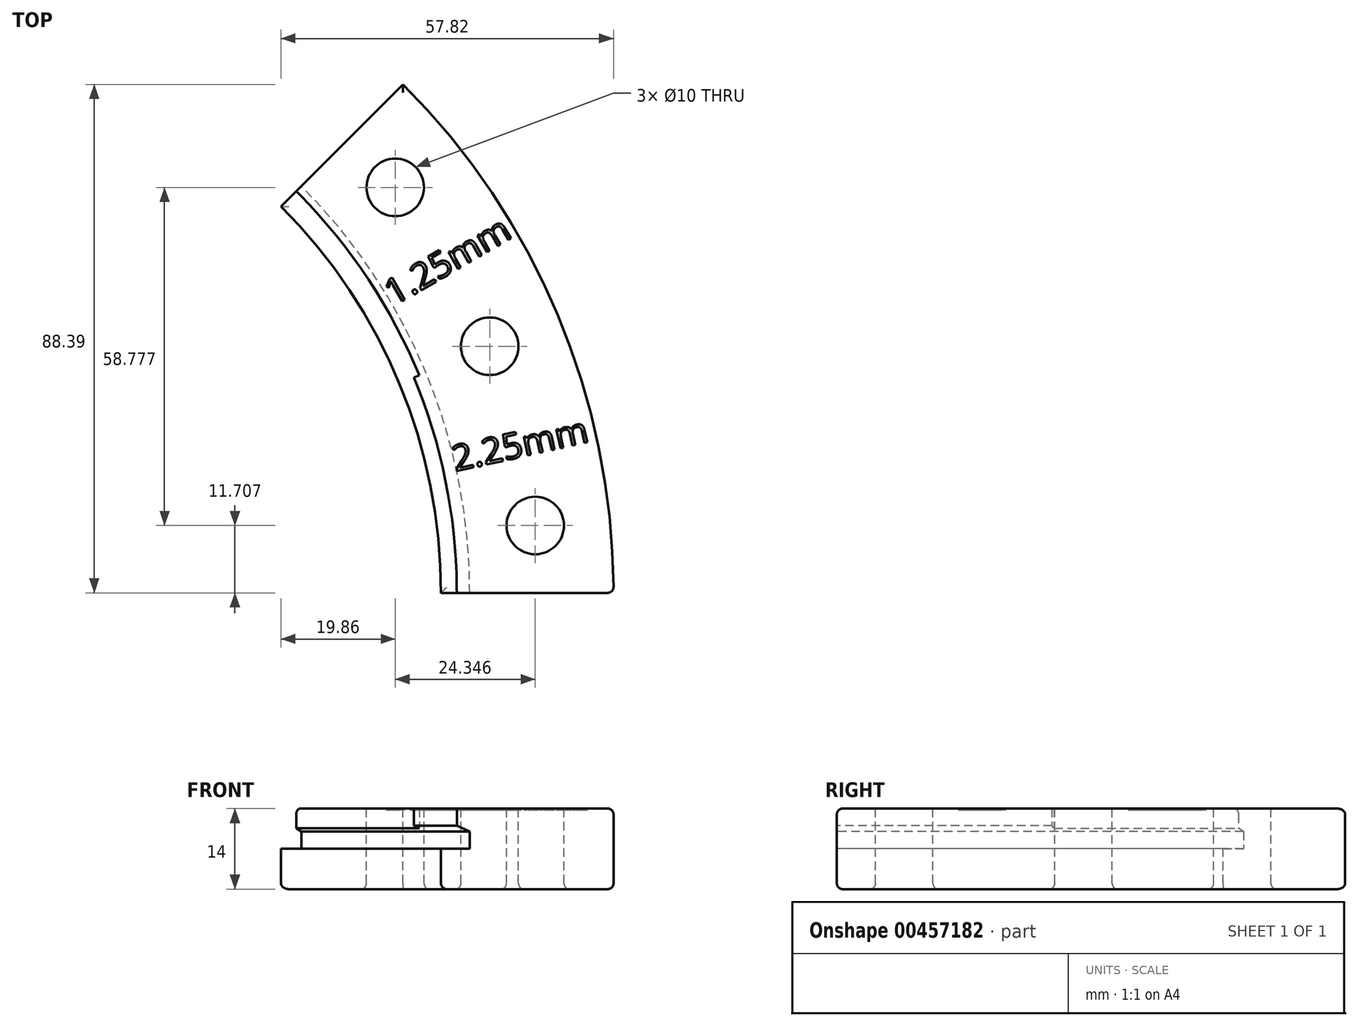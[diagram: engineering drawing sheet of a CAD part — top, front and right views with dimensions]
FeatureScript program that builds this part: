
annotation { "Feature Type Name" : "Feature", "Feature Type Description" : "" }
export const myFeature = defineFeature(function(context is Context, id is Id, definition is map)
    precondition{}
    {
        {
            var Q0;
            Q0=qCreatedBy(makeId("Top.planeOp"),FACE);
            var sketch = newSketch(context, id + "F0", { "sketchPlane" : qUnion([Q0])});
            skCircle(sketch, "E0", {"center": v(0, 0) * mm, "radius": 100 * mm});
            skSolve(sketch);
        }
        {
            var Q0;
            Q0=qCreatedBy(makeId("Front.planeOp"),FACE);
            var sketch = newSketch(context, id + "F1", { "sketchPlane" : qUnion([Q0])});
            skLineSegment(sketch, "E1.0", {"start": v(-100, 0) * mm, "end": v(100, 0) * mm});
            skLineSegment(sketch, "E2", {"start": v(100, 4) * mm, "end": v(97.75, 4) * mm});
            skLineSegment(sketch, "E3", {"start": v(125, 4) * mm, "end": v(100, 4) * mm});
            skLineSegment(sketch, "E4", {"start": v(100, 0) * mm, "end": v(100, -3) * mm});
            skLineSegment(sketch, "E5", {"start": v(100, -10) * mm, "end": v(125, -10) * mm});
            skLineSegment(sketch, "E6", {"start": v(125, -10) * mm, "end": v(125, 4) * mm});
            skLineSegment(sketch, "E7", {"start": v(0, 0) * mm, "end": v(0, 50.74) * mm});
            skLineSegment(sketch, "E8", {"start": v(100, -10) * mm, "end": v(95, -10) * mm});
            skLineSegment(sketch, "E9", {"start": v(95, -10) * mm, "end": v(95, -3) * mm});
            skLineSegment(sketch, "E10", {"start": v(95, -3) * mm, "end": v(100, -3) * mm});
            skLineSegment(sketch, "E11", {"start": v(97.75, 4) * mm, "end": v(97.75, 1) * mm});
            skLineSegment(sketch, "E12", {"start": v(100, 0) * mm, "end": v(97.75, 1) * mm});
            skSolve(sketch);
        }
        {
            var Q0;
            Q0=makeQuery(id+"F1.imprint","IMPRINT",FACE,{"disambiguationData":[TD([[makeQuery(id+"F1.imprint","IMPRINT",EDGE,{"derivedFrom":sQuery(id+"F1.wireOp",EDGE,"E2")}),1.0]])]});
            var Q1;
            Q1=sQuery(id+"F1.wireOp",EDGE,"E7");
            revolve(context, id + "F2", {"entities" : qUnion([Q0]), "axis" : qUnion([Q1]), "revolveType" : RevolveType.ONE_DIRECTION, "angle" : 45 * degree});
        }
        {
            var Q0;
            Q0=makeQuery(id+"F2.opRevolve","CAP_FACE",FACE,{"disambiguationData":[OSD([sQuery(id+"F1.wireOp",EDGE,"E2"),sQuery(id+"F1.wireOp",EDGE,"E3"),sQuery(id+"F1.wireOp",EDGE,"E4"),sQuery(id+"F1.wireOp",EDGE,"E5"),sQuery(id+"F1.wireOp",EDGE,"E6"),sQuery(id+"F1.wireOp",EDGE,"E8"),sQuery(id+"F1.wireOp",EDGE,"E9"),sQuery(id+"F1.wireOp",EDGE,"E10"),sQuery(id+"F1.wireOp",EDGE,"E11"),sQuery(id+"F1.wireOp",EDGE,"E12")])],"isStart":false});
            var sketch = newSketch(context, id + "F3", { "sketchPlane" : qUnion([Q0])});
            skLineSegment(sketch, "E13", {"start": v(0, 0) * mm, "end": v(0, 46.88) * mm});
            skLineSegment(sketch, "E14.0", {"start": v(-98.75, 0.56) * mm, "end": v(-97.75, 1) * mm});
            skLineSegment(sketch, "E15.0", {"start": v(-97.75, 4) * mm, "end": v(-97.75, 1) * mm});
            skLineSegment(sketch, "E16.0", {"start": v(-98.75, 4) * mm, "end": v(-97.75, 4) * mm});
            skLineSegment(sketch, "E17", {"start": v(-98.75, 4) * mm, "end": v(-98.75, 0.56) * mm});
            skLineSegment(sketch, "E18", {"start": v(-97.75, 4) * mm, "end": v(-98.75, 4) * mm});
            skPoint(sketch, "E19.start.orphan", {"position": v(-100, 0) * mm});
            skPoint(sketch, "E20.orphan", {"position": v(-125, 4) * mm});
            skSolve(sketch);
        }
        {
            var Q0;
            Q0=makeQuery(id+"F3.imprint","IMPRINT",FACE,{"disambiguationData":[TD([[makeQuery(id+"F3.imprint","IMPRINT",EDGE,{"derivedFrom":sQuery(id+"F3.wireOp",EDGE,"E15.0")}),-1.0]])]});
            var Q1;
            Q1=sQuery(id+"F3.wireOp",EDGE,"E13");
            revolve(context, id + "F4", {"operationType" : NewBodyOperationType.REMOVE, "entities" : qUnion([Q0]), "axis" : qUnion([Q1]), "revolveType" : RevolveType.ONE_DIRECTION, "oppositeDirection" : true, "angle" : 22.5 * degree});
        }
        {
            var Q0;
            Q0=makeQuery(id+"F2.opRevolve","SWEPT_FACE",FACE,{"disambiguationData":[OSD([sQuery(id+"F1.wireOp",EDGE,"E2"),sQuery(id+"F1.wireOp",EDGE,"E3")])]});
            var sketch = newSketch(context, id + "F5", { "sketchPlane" : qUnion([Q0])});
            skCircle(sketch, "E21", {"center": v(87.04, 70.48) * mm, "radius": 5 * mm});
            skCircle(sketch, "E22", {"center": v(111.39, 11.7) * mm, "radius": 5 * mm});
            skCircle(sketch, "E23", {"center": v(103.47, 42.86) * mm, "radius": 5 * mm});
            skText(sketch, "E24", { "text": "2.25mm", "fontName": "OpenSans-Regular.ttf"});
            skText(sketch, "E25", { "text": "1.25mm", "fontName": "OpenSans-Regular.ttf"});
            const initialGuessF5  = {"E24": [0.09749, 0.0211, 0.97648, 0.21563, 0.0045], "E25": [0.0868, 0.04986, 0.86603, 0.5, 0.0045]};
            skSetInitialGuess(sketch, initialGuessF5);
            skSolve(sketch);
        }
        {
            var Q0;
            Q0=makeQuery(id+"F5.imprint","IMPRINT",FACE,{"disambiguationData":[TD([[makeQuery(id+"F5.imprint","IMPRINT",EDGE,{"derivedFrom":sQuery(id+"F5.wireOp",EDGE,"E21")}),1.0]])]});
            var Q1;
            Q1=makeQuery(id+"F5.imprint","IMPRINT",FACE,{"disambiguationData":[TD([[makeQuery(id+"F5.imprint","IMPRINT",EDGE,{"derivedFrom":sQuery(id+"F5.wireOp",EDGE,"E23")}),1.0]])]});
            var Q2;
            Q2=makeQuery(id+"F5.imprint","IMPRINT",FACE,{"disambiguationData":[TD([[makeQuery(id+"F5.imprint","IMPRINT",EDGE,{"derivedFrom":sQuery(id+"F5.wireOp",EDGE,"E22")}),1.0]])]});
            extrude(context, id + "F6", {"entities" : qUnion([Q0, Q1, Q2]), "operationType" : NewBodyOperationType.REMOVE, "endBound" : BoundingType.THROUGH_ALL, "oppositeDirection" : true, "depth" : 25 * mm});
        }
        {
            var Q0;
            Q0 = qSketchRegion(id + "F5", true);
            extrude(context, id + "F7", {"entities" : qUnion([Q0]), "operationType" : NewBodyOperationType.REMOVE, "oppositeDirection" : true, "depth" : .25 * mm});
        }
        {
            var Q0;
            Q0=makeQuery(id+"F2.opRevolve","CAP_EDGE",EDGE,{"disambiguationData":[OSD([sQuery(id+"F1.wireOp",EDGE,"E2"),sQuery(id+"F1.wireOp",EDGE,"E3")])],"isStart":true});
            var Q1;
            Q1=makeQuery(id+"F2.opRevolve","SWEPT_EDGE",EDGE,{"disambiguationData":[OSD([sQuery(id+"F1.wireOp",EDGE,"E3"),sQuery(id+"F1.wireOp",EDGE,"E6")])]});
            var Q2;
            Q2=makeQuery(id+"F2.opRevolve","CAP_EDGE",EDGE,{"disambiguationData":[OSD([sQuery(id+"F1.wireOp",EDGE,"E2"),sQuery(id+"F1.wireOp",EDGE,"E3")])],"isStart":false});
            var Q3;
            Q3=makeQuery(id+"F2.opRevolve","CAP_EDGE",EDGE,{"disambiguationData":[OSD([sQuery(id+"F1.wireOp",EDGE,"E6")])],"isStart":true});
            var Q4;
            Q4=makeQuery(id+"F2.opRevolve","CAP_EDGE",EDGE,{"disambiguationData":[OSD([sQuery(id+"F1.wireOp",EDGE,"E5"),sQuery(id+"F1.wireOp",EDGE,"E8")])],"isStart":true});
            var Q5;
            Q5=makeQuery(id+"F2.opRevolve","SWEPT_EDGE",EDGE,{"disambiguationData":[OSD([sQuery(id+"F1.wireOp",EDGE,"E5"),sQuery(id+"F1.wireOp",EDGE,"E6")])]});
            var Q6;
            Q6=makeQuery(id+"F2.opRevolve","SWEPT_EDGE",EDGE,{"disambiguationData":[OSD([sQuery(id+"F1.wireOp",EDGE,"E8"),sQuery(id+"F1.wireOp",EDGE,"E9")])]});
            var Q7;
            Q7=makeQuery(id+"F2.opRevolve","CAP_EDGE",EDGE,{"disambiguationData":[OSD([sQuery(id+"F1.wireOp",EDGE,"E5"),sQuery(id+"F1.wireOp",EDGE,"E8")])],"isStart":false});
            var Q8;
            Q8=makeQuery(id+"F6.boolean.opBoolean","COPY",EDGE,{"derivedFrom":makeQuery(id+"F6.opExtrude","CAP_EDGE",EDGE,{"disambiguationData":[OSD([sQuery(id+"F5.wireOp",EDGE,"E21")])],"isStart":true})});
            var Q9;
            Q9=makeQuery(id+"F6.boolean.opBoolean","COPY",EDGE,{"derivedFrom":makeQuery(id+"F6.opExtrude","CAP_EDGE",EDGE,{"disambiguationData":[OSD([sQuery(id+"F5.wireOp",EDGE,"E23")])],"isStart":true})});
            var Q10;
            Q10=makeQuery(id+"F6.boolean.opBoolean","COPY",EDGE,{"derivedFrom":makeQuery(id+"F6.opExtrude","CAP_EDGE",EDGE,{"disambiguationData":[OSD([sQuery(id+"F5.wireOp",EDGE,"E22")])],"isStart":true})});
            var Q11;
            Q11=makeQuery(id+"F6.boolean.opBoolean","INTERSECT",EDGE,{"derivedFrom":[makeQuery(id+"F2.opRevolve","SWEPT_FACE",FACE,{"disambiguationData":[OSD([sQuery(id+"F1.wireOp",EDGE,"E5"),sQuery(id+"F1.wireOp",EDGE,"E8")])]}),makeQuery(id+"F6.opExtrude","SWEPT_FACE",FACE,{"disambiguationData":[OSD([sQuery(id+"F5.wireOp",EDGE,"E22")])]})]});
            var Q12;
            Q12=makeQuery(id+"F6.boolean.opBoolean","INTERSECT",EDGE,{"derivedFrom":[makeQuery(id+"F2.opRevolve","SWEPT_FACE",FACE,{"disambiguationData":[OSD([sQuery(id+"F1.wireOp",EDGE,"E5"),sQuery(id+"F1.wireOp",EDGE,"E8")])]}),makeQuery(id+"F6.opExtrude","SWEPT_FACE",FACE,{"disambiguationData":[OSD([sQuery(id+"F5.wireOp",EDGE,"E23")])]})]});
            var Q13;
            Q13=makeQuery(id+"F6.boolean.opBoolean","INTERSECT",EDGE,{"derivedFrom":[makeQuery(id+"F2.opRevolve","SWEPT_FACE",FACE,{"disambiguationData":[OSD([sQuery(id+"F1.wireOp",EDGE,"E5"),sQuery(id+"F1.wireOp",EDGE,"E8")])]}),makeQuery(id+"F6.opExtrude","SWEPT_FACE",FACE,{"disambiguationData":[OSD([sQuery(id+"F5.wireOp",EDGE,"E21")])]})]});
            fillet(context, id + "F8", {"entities" : qUnion([Q0, Q1, Q2, Q3, Q4, Q5, Q6, Q7, Q8, Q9, Q10, Q11, Q12, Q13]), "radius" : 1 * mm, "tangentPropagation" : true, "allowEdgeOverflow" : false});
        }
    });
